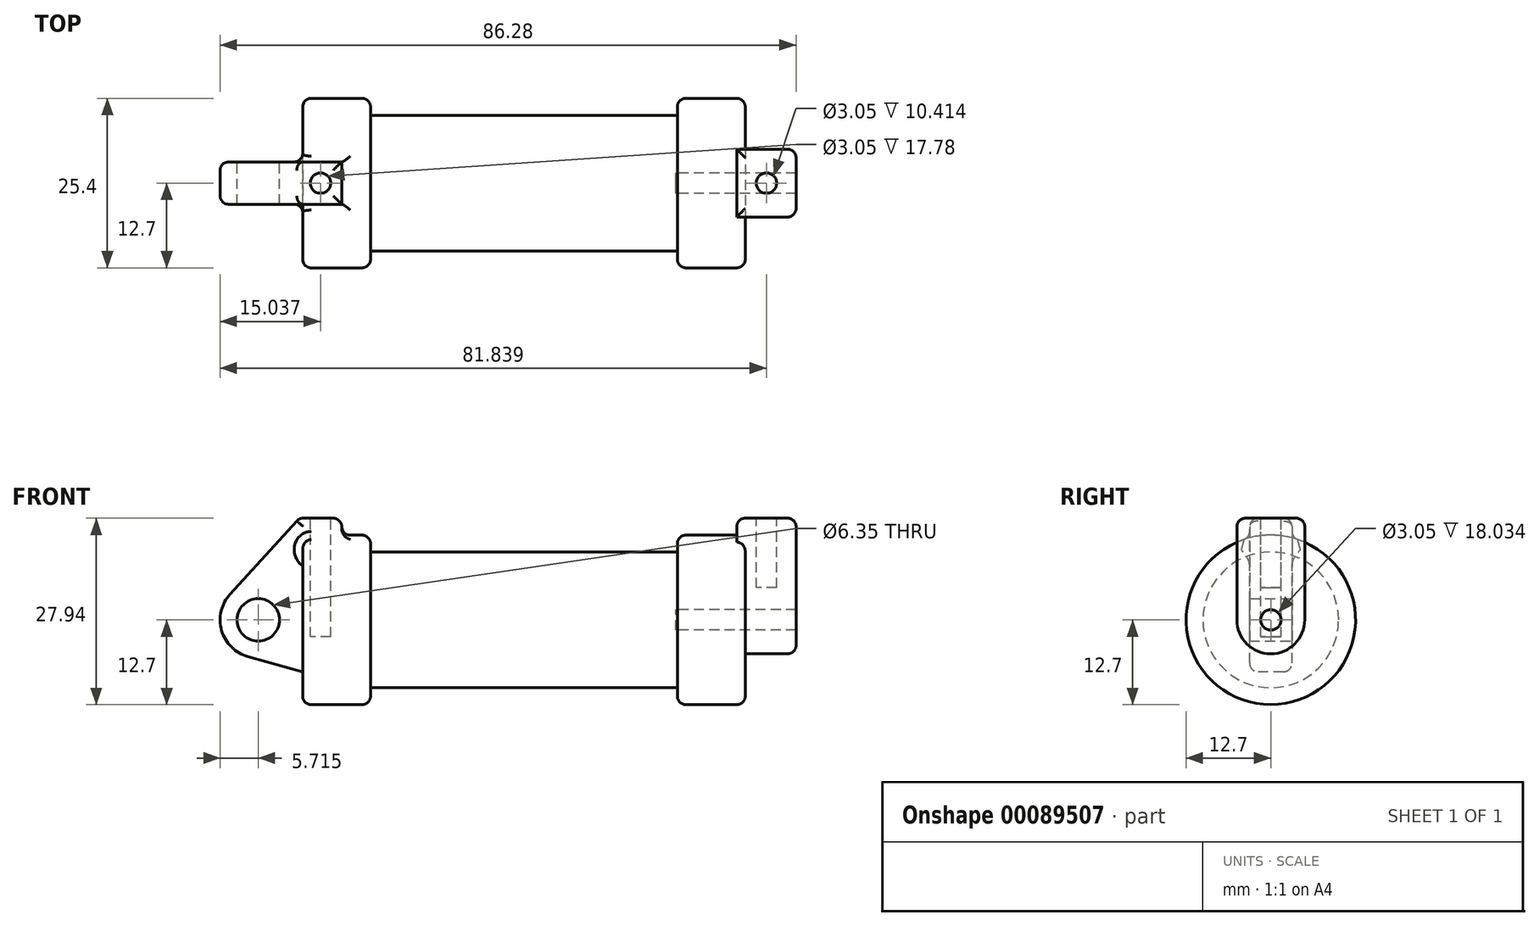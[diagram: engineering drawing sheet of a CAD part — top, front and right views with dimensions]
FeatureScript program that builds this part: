
annotation { "Feature Type Name" : "Feature", "Feature Type Description" : "" }
export const myFeature = defineFeature(function(context is Context, id is Id, definition is map)
    precondition{}
    {
        {
            var Q0;
            Q0=qCreatedBy(makeId("Front.planeOp"),FACE);
            var sketch = newSketch(context, id + "F0", { "sketchPlane" : qUnion([Q0])});
            skLineSegment(sketch, "E0", {"start": v(0, 0) * mm, "end": v(0, 12.7) * mm});
            skLineSegment(sketch, "E1", {"start": v(0, 12.7) * mm, "end": v(10.16, 12.7) * mm});
            skLineSegment(sketch, "E2", {"start": v(10.16, 12.7) * mm, "end": v(10.16, 10.16) * mm});
            skLineSegment(sketch, "E3", {"start": v(10.16, 10.16) * mm, "end": v(56.13, 10.16) * mm});
            skLineSegment(sketch, "E4", {"start": v(56.13, 10.16) * mm, "end": v(56.13, 12.7) * mm});
            skLineSegment(sketch, "E5", {"start": v(56.13, 12.7) * mm, "end": v(66.3, 12.7) * mm});
            skLineSegment(sketch, "E6", {"start": v(66.3, 12.7) * mm, "end": v(66.3, 0) * mm});
            skLineSegment(sketch, "E7", {"start": v(66.3, 0) * mm, "end": v(0, 0) * mm});
            skLineSegment(sketch, "E8", {"start": v(5.84, 15.24) * mm, "end": v(-0.5, 15.24) * mm});
            skLineSegment(sketch, "E9", {"start": v(-0.5, 15.24) * mm, "end": v(-10.88, 3.85) * mm});
            skLineSegment(sketch, "E10", {"start": v(0, 0) * mm, "end": v(-6.65, 0) * mm});
            skCircle(sketch, "E11", {"center": v(-6.65, 0) * mm, "radius": 5.72 * mm});
            skCircle(sketch, "E12", {"center": v(-6.65, 0) * mm, "radius": 3.18 * mm});
            skLineSegment(sketch, "E13", {"start": v(5.84, 15.24) * mm, "end": v(5.84, -9.4) * mm});
            skLineSegment(sketch, "E14", {"start": v(5.84, -9.4) * mm, "end": v(-8.18, -5.5) * mm});
            skSolve(sketch);
        }
        {
            var Q0;
            {var subQ3=sQuery(id+"F0.wireOp",EDGE,"E0");Q0=makeQuery(id+"F0.imprint","IMPRINT",FACE,{"disambiguationData":[TD([[makeQuery(id+"F0.imprint","IMPRINT",EDGE,{"derivedFrom":subQ3}),1.0]])]});}
            var Q1;
            {var subQ0=sQuery(id+"F0.wireOp",EDGE,"E0");Q1=makeQuery(id+"F0.imprint","IMPRINT",FACE,{"disambiguationData":[TD([[makeQuery(id+"F0.imprint","IMPRINT",EDGE,{"derivedFrom":subQ0}),-1.0]])]});}
            var Q2;
            {var subQ0=sQuery(id+"F0.wireOp",EDGE,"E14");Q2=makeQuery(id+"F0.imprint","IMPRINT",FACE,{"disambiguationData":[TD([[makeQuery(id+"F0.imprint","IMPRINT",EDGE,{"derivedFrom":subQ0}),-1.0]])]});}
            var Q3;
            {var subQ4=sQuery(id+"F0.wireOp",EDGE,"E12");Q3=makeQuery(id+"F0.imprint","IMPRINT",FACE,{"disambiguationData":[TD([[makeQuery(id+"F0.imprint","IMPRINT",EDGE,{"derivedFrom":subQ4}),-1.0]])]});}
            extrude(context, id + "F1", {"entities" : qUnion([Q0, Q1, Q2, Q3]), "endBound" : BoundingType.SYMMETRIC, "depth" : 6.35 * mm});
        }
        {
            var Q0;
            {var subQ0=sQuery(id+"F0.wireOp",EDGE,"E2");Q0=makeQuery(id+"F0.imprint","IMPRINT",FACE,{"disambiguationData":[TD([[makeQuery(id+"F0.imprint","IMPRINT",EDGE,{"derivedFrom":subQ0}),-1.0]])]});}
            var Q1;
            {var subQ0=sQuery(id+"F0.wireOp",EDGE,"E0");Q1=makeQuery(id+"F0.imprint","IMPRINT",FACE,{"disambiguationData":[TD([[makeQuery(id+"F0.imprint","IMPRINT",EDGE,{"derivedFrom":subQ0}),-1.0]])]});}
            var Q2;
            Q2=sQuery(id+"F0.wireOp",EDGE,"E7");
            revolve(context, id + "F2", {"operationType" : NewBodyOperationType.ADD, "entities" : qUnion([Q0, Q1]), "axis" : qUnion([Q2]), "revolveType" : RevolveType.FULL});
        }
        {
            var Q0;
            Q0=makeQuery(id+"F2.opRevolve","SWEPT_FACE",FACE,{"disambiguationData":[OSD([sQuery(id+"F0.wireOp",EDGE,"E6")])]});
            var sketch = newSketch(context, id + "F3", { "sketchPlane" : qUnion([Q0])});
            skCircle(sketch, "E15", {"center": v(0, 0) * mm, "radius": 1.52 * mm});
            skCircle(sketch, "E16", {"center": v(0, 0) * mm, "radius": 5.08 * mm});
            skLineSegment(sketch, "E17", {"start": v(5.08, 0) * mm, "end": v(5.08, 15.24) * mm});
            skLineSegment(sketch, "E18", {"start": v(-5.08, 0) * mm, "end": v(-5.08, 15.24) * mm});
            skLineSegment(sketch, "E19", {"start": v(-5.08, 15.24) * mm, "end": v(5.08, 15.24) * mm});
            skSolve(sketch);
        }
        {
            var Q0;
            Q0 = qSketchRegion(id + "F3", true);
            extrude(context, id + "F4", {"entities" : qUnion([Q0]), "operationType" : NewBodyOperationType.ADD, "depth" : 7.62 * mm});
        }
        {
            var Q0;
            Q0 = qSketchRegion(id + "F3", true);
            extrude(context, id + "F5", {"entities" : qUnion([Q0]), "operationType" : NewBodyOperationType.ADD, "oppositeDirection" : true, "depth" : 1.27 * mm});
        }
        {
            var Q0;
            Q0=makeQuery(id+"F4.boolean.opBoolean","SPLIT",FACE,{"disambiguationData":[TD([makeQuery(id+"F4.opExtrude","SWEPT_FACE",FACE,{"disambiguationData":[OSD([sQuery(id+"F3.wireOp",EDGE,"E15")])]})])],"derivedFrom":makeQuery(id+"F2.opRevolve","SWEPT_FACE",FACE,{"disambiguationData":[OSD([sQuery(id+"F0.wireOp",EDGE,"E6")])]})});
            extrude(context, id + "F6", {"entities" : qUnion([Q0]), "operationType" : NewBodyOperationType.REMOVE, "oppositeDirection" : true, "depth" : 10.4 * mm});
        }
        {
            var Q0;
            {var subQ0=sQuery(id+"F3.wireOp",EDGE,"E19");Q0=makeQuery(id+"F5.boolean.opBoolean","MERGE",FACE,{"derivedFrom":[makeQuery(id+"F4.opExtrude","SWEPT_FACE",FACE,{"disambiguationData":[OSD([subQ0])]}),makeQuery(id+"F5.opExtrude","SWEPT_FACE",FACE,{"disambiguationData":[OSD([subQ0])]})]});}
            var sketch = newSketch(context, id + "F7", { "sketchPlane" : qUnion([Q0])});
            skLineSegment(sketch, "E20", {"start": v(69.47, 5.08) * mm, "end": v(69.47, -5.08) * mm, "construction": true});
            skLineSegment(sketch, "E21", {"start": v(65.02, 0) * mm, "end": v(73.91, 0) * mm, "construction": true});
            skCircle(sketch, "E22", {"center": v(69.47, 0) * mm, "radius": 1.52 * mm});
            skLineSegment(sketch, "E23", {"start": v(2.5, 2.96) * mm, "end": v(2.5, -3.02) * mm, "construction": true});
            skLineSegment(sketch, "E24", {"start": v(-0.45, -0.06) * mm, "end": v(5.87, -0.06) * mm, "construction": true});
            skCircle(sketch, "E25", {"center": v(2.5, -0.06) * mm, "radius": 1.52 * mm});
            skSolve(sketch);
        }
        {
            var Q0;
            Q0=makeQuery(id+"F7.imprint","IMPRINT",FACE,{"disambiguationData":[TD([[makeQuery(id+"F7.imprint","IMPRINT",EDGE,{"derivedFrom":sQuery(id+"F7.wireOp",EDGE,"E22")}),1.0]])]});
            extrude(context, id + "F8", {"entities" : qUnion([Q0]), "operationType" : NewBodyOperationType.REMOVE, "oppositeDirection" : true, "depth" : 10.4 * mm});
        }
        {
            var Q0;
            Q0=makeQuery(id+"F1.opExtrude","SWEPT_FACE",FACE,{"disambiguationData":[OSD([sQuery(id+"F0.wireOp",EDGE,"E8")])]});
            var sketch = newSketch(context, id + "F9", { "sketchPlane" : qUnion([Q0])});
            skLineSegment(sketch, "E26", {"start": v(2.67, 3.18) * mm, "end": v(2.67, -3.18) * mm, "construction": true});
            skLineSegment(sketch, "E27", {"start": v(-0.5, 0) * mm, "end": v(5.84, 0) * mm, "construction": true});
            skCircle(sketch, "E28", {"center": v(2.67, 0) * mm, "radius": 1.52 * mm});
            skSolve(sketch);
        }
        {
            var Q0;
            Q0 = qSketchRegion(id + "F9", true);
            extrude(context, id + "F10", {"entities" : qUnion([Q0]), "operationType" : NewBodyOperationType.REMOVE, "oppositeDirection" : true, "depth" : 17.78 * mm});
        }
        {
            var Q0;
            Q0=makeQuery(id+"F1.opExtrude","SWEPT_FACE",FACE,{"disambiguationData":[OSD([sQuery(id+"F0.wireOp",EDGE,"E11")])]});
            var Q1;
            Q1=makeQuery(id+"F4.opExtrude","CAP_EDGE",EDGE,{"disambiguationData":[OSD([sQuery(id+"F3.wireOp",EDGE,"E19")])],"isStart":false});
            fillet(context, id + "F11", {"entities" : qUnion([Q0, Q1]), "radius" : 1.27 * mm, "tangentPropagation" : true, "allowEdgeOverflow" : false});
        }
        {
            var Q0;
            Q0=makeQuery(id+"F2.opRevolve","SWEPT_FACE",FACE,{"disambiguationData":[OSD([sQuery(id+"F0.wireOp",EDGE,"E1")])]});
            fillet(context, id + "F12", {"entities" : qUnion([Q0]), "radius" : 1.27 * mm, "tangentPropagation" : true, "allowEdgeOverflow" : false});
        }
        {
            var Q0;
            Q0=makeQuery(id+"F1.opExtrude","CAP_EDGE",EDGE,{"disambiguationData":[OSD([sQuery(id+"F0.wireOp",EDGE,"E8")])],"isStart":false});
            var Q1;
            Q1=makeQuery(id+"F1.opExtrude","SWEPT_EDGE",EDGE,{"disambiguationData":[OSD([sQuery(id+"F0.wireOp",EDGE,"E8"),sQuery(id+"F0.wireOp",EDGE,"E13")])]});
            var Q2;
            Q2=makeQuery(id+"F1.opExtrude","SWEPT_EDGE",EDGE,{"disambiguationData":[OSD([sQuery(id+"F0.wireOp",EDGE,"E8"),sQuery(id+"F0.wireOp",EDGE,"E9")])]});
            var Q3;
            Q3=makeQuery(id+"F1.opExtrude","CAP_EDGE",EDGE,{"disambiguationData":[OSD([sQuery(id+"F0.wireOp",EDGE,"E8")])],"isStart":true});
            fillet(context, id + "F13", {"entities" : qUnion([Q0, Q1, Q2, Q3]), "radius" : 1.27 * mm, "tangentPropagation" : true, "allowEdgeOverflow" : false});
        }
        {
            var Q0;
            {var subQ0=sQuery(id+"F3.wireOp",EDGE,"E19");var subQ1=sQuery(id+"F3.wireOp",EDGE,"E17");Q0=makeQuery(id+"F5.boolean.opBoolean","MERGE",EDGE,{"derivedFrom":[makeQuery(id+"F4.opExtrude","SWEPT_EDGE",EDGE,{"disambiguationData":[OSD([subQ1,subQ0])]}),makeQuery(id+"F5.opExtrude","SWEPT_EDGE",EDGE,{"disambiguationData":[OSD([subQ1,subQ0])]})]});}
            var Q1;
            {var subQ0=sQuery(id+"F3.wireOp",EDGE,"E19");var subQ1=sQuery(id+"F3.wireOp",EDGE,"E18");Q1=makeQuery(id+"F5.boolean.opBoolean","MERGE",EDGE,{"derivedFrom":[makeQuery(id+"F4.opExtrude","SWEPT_EDGE",EDGE,{"disambiguationData":[OSD([subQ1,subQ0])]}),makeQuery(id+"F5.opExtrude","SWEPT_EDGE",EDGE,{"disambiguationData":[OSD([subQ1,subQ0])]})]});}
            var Q2;
            Q2=makeQuery(id+"F5.opExtrude","CAP_EDGE",EDGE,{"disambiguationData":[OSD([sQuery(id+"F3.wireOp",EDGE,"E19")])],"isStart":false});
            var Q3;
            Q3=makeQuery(id+"F2.opRevolve","SWEPT_EDGE",EDGE,{"disambiguationData":[OSD([sQuery(id+"F0.wireOp",EDGE,"E4"),sQuery(id+"F0.wireOp",EDGE,"E5")])]});
            var Q4;
            Q4=makeQuery(id+"F4.boolean.opBoolean","SPLIT",EDGE,{"disambiguationData":[OD(1.0)],"derivedFrom":makeQuery(id+"F2.opRevolve","SWEPT_EDGE",EDGE,{"disambiguationData":[OSD([sQuery(id+"F0.wireOp",EDGE,"E5"),sQuery(id+"F0.wireOp",EDGE,"E6")])]})});
            fillet(context, id + "F14", {"entities" : qUnion([Q0, Q1, Q2, Q3, Q4]), "radius" : 1.27 * mm, "tangentPropagation" : true, "allowEdgeOverflow" : false});
        }
    });
